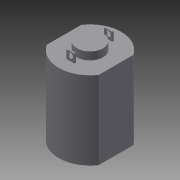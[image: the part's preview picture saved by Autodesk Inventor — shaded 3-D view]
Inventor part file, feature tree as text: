
AUTODESK INVENTOR PART (.ipt)
format: ipt  version: 2014 SP1 (Build 180222100, 222)  size: 118,784 bytes
history: native  units: mm
features: extrude x4, sketch x4, fillet x1, mirror x1
ambient origin geometry x8: Origin, YZ Plane, XZ Plane, XY Plane, X Axis, Y Axis, Z Axis, Center Point
bodies: Solid1 (feature_tree)
feature tree (10):
  extrude  "Extrusion1"  Depth=10.0mm
  extrude  "Extrusion2"  Depth=15.0mm
  extrude  "Extrusion3"  Depth=1.5mm
  extrude  "Extrusion4"  Depth=1.55mm
  fillet  "Fillet1"  Radius=1.65mm
  mirror  "Mirror1"
  sketch  "Sketch1"  dims[d0=12.0mm d1=10.0mm]
  sketch  "Sketch2"  dims[d2=15.0mm d3=0.0mm d4=5.0mm]
  sketch  "Sketch3"  dims[d5=1.5mm d6=0.0mm d7=3.775mm]
  sketch  "Sketch4"  dims[d8=0.3mm d9=1.55mm d10=1.65mm d11=0.0mm d12=1.0mm d13=0.7mm d14=1.65mm d15=0.0mm d16=0.25mm]
